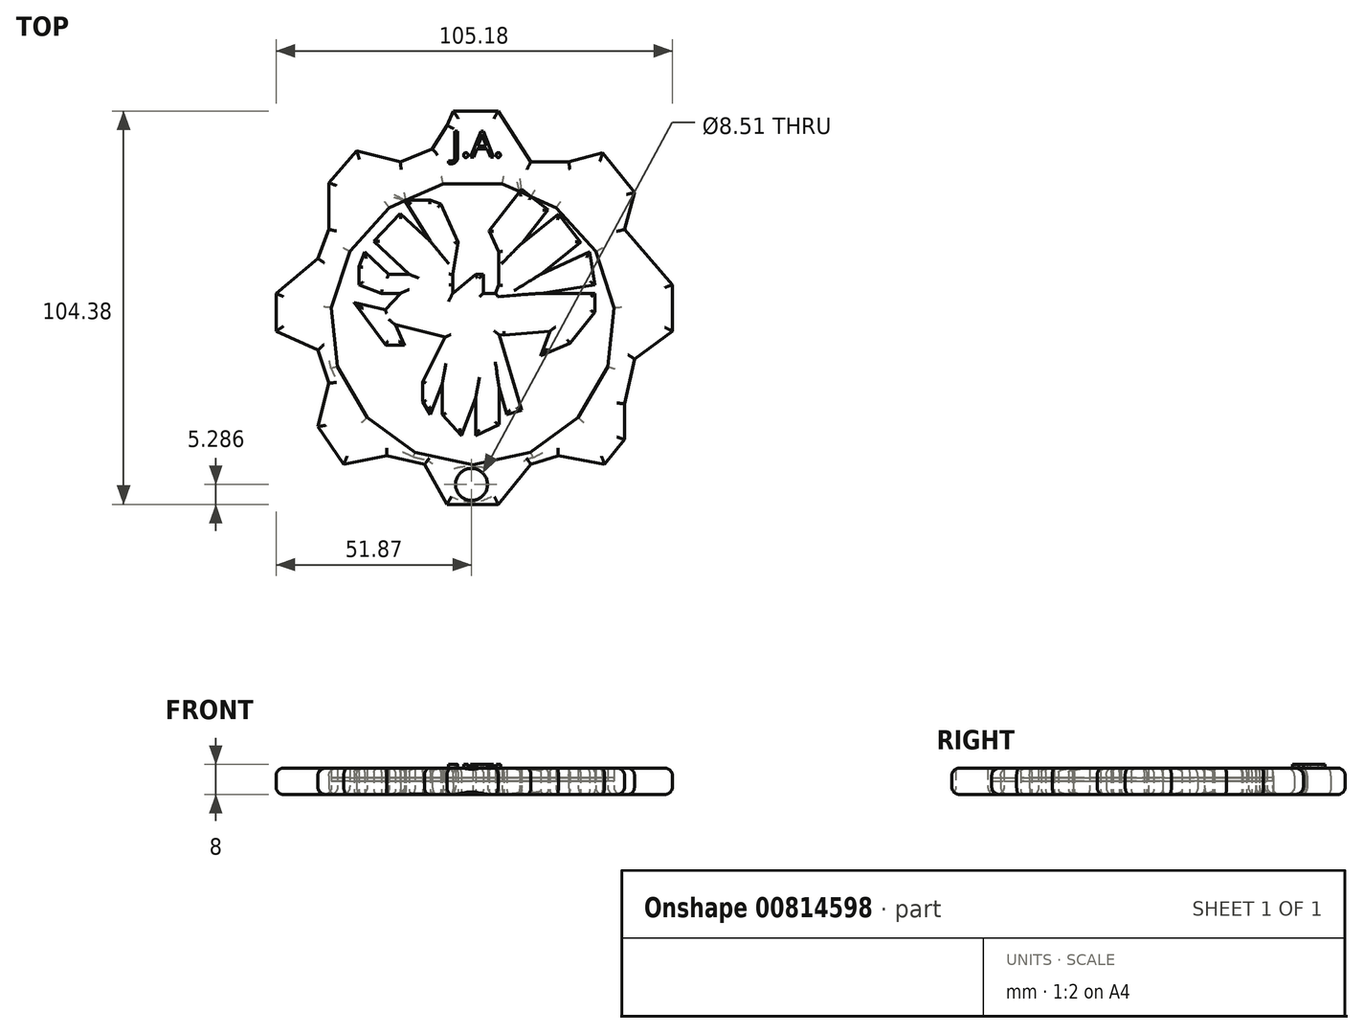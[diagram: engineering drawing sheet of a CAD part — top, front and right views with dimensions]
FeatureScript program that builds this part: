
annotation { "Feature Type Name" : "Feature", "Feature Type Description" : "" }
export const myFeature = defineFeature(function(context is Context, id is Id, definition is map)
    precondition{}
    {
        {
            var Q0;
            Q0=qCreatedBy(makeId("Top.planeOp"),FACE);
            var sketch = newSketch(context, id + "F0", { "sketchPlane" : qUnion([Q0])});
            skLineSegment(sketch, "E0", {"start": v(-27.88, 46.11) * mm, "end": v(-15.99, 46.11) * mm});
            skLineSegment(sketch, "E1", {"start": v(-15.99, 46.11) * mm, "end": v(-7.27, 32.64) * mm});
            skLineSegment(sketch, "E2", {"start": v(-7.27, 32.64) * mm, "end": v(2.77, 32.64) * mm});
            skLineSegment(sketch, "E3", {"start": v(2.77, 32.64) * mm, "end": v(11.76, 35.01) * mm});
            skLineSegment(sketch, "E4", {"start": v(11.76, 35.01) * mm, "end": v(20.22, 24.44) * mm});
            skLineSegment(sketch, "E5", {"start": v(20.22, 24.44) * mm, "end": v(17.57, 14.67) * mm});
            skLineSegment(sketch, "E6", {"start": v(17.57, 14.67) * mm, "end": v(30.26, 0) * mm});
            skLineSegment(sketch, "E7", {"start": v(30.26, 0) * mm, "end": v(30.26, -12.29) * mm});
            skLineSegment(sketch, "E8", {"start": v(30.26, -12.29) * mm, "end": v(20.22, -19.69) * mm});
            skLineSegment(sketch, "E9", {"start": v(20.22, -19.69) * mm, "end": v(17.57, -31.58) * mm});
            skLineSegment(sketch, "E10", {"start": v(17.57, -31.58) * mm, "end": v(17.57, -41.1) * mm});
            skLineSegment(sketch, "E11", {"start": v(17.57, -41.1) * mm, "end": v(12.29, -47.7) * mm});
            skLineSegment(sketch, "E12", {"start": v(12.29, -47.7) * mm, "end": v(0, -45.32) * mm});
            skLineSegment(sketch, "E13", {"start": v(0, -45.32) * mm, "end": v(-7.27, -47.7) * mm});
            skLineSegment(sketch, "E14", {"start": v(-7.27, -47.7) * mm, "end": v(-15.99, -58.27) * mm});
            skLineSegment(sketch, "E15", {"start": v(-15.99, -58.27) * mm, "end": v(-29.56, -58.27) * mm});
            skLineSegment(sketch, "E16", {"start": v(-29.56, -58.27) * mm, "end": v(-35.54, -47.7) * mm});
            skLineSegment(sketch, "E17", {"start": v(-35.54, -47.7) * mm, "end": v(-45.59, -45.32) * mm});
            skLineSegment(sketch, "E18", {"start": v(-45.59, -45.32) * mm, "end": v(-56.95, -47.7) * mm});
            skLineSegment(sketch, "E19", {"start": v(-56.95, -47.7) * mm, "end": v(-63.82, -37.66) * mm});
            skLineSegment(sketch, "E20", {"start": v(-63.82, -37.66) * mm, "end": v(-60.91, -26.03) * mm});
            skLineSegment(sketch, "E21", {"start": v(-60.91, -26.03) * mm, "end": v(-63.82, -17.3) * mm});
            skLineSegment(sketch, "E22", {"start": v(-63.82, -17.3) * mm, "end": v(-74.92, -12.29) * mm});
            skLineSegment(sketch, "E23", {"start": v(-74.92, -12.29) * mm, "end": v(-74.92, -2.25) * mm});
            skLineSegment(sketch, "E24", {"start": v(-74.92, -2.25) * mm, "end": v(-63.82, 7) * mm});
            skLineSegment(sketch, "E25", {"start": v(-63.82, 7) * mm, "end": v(-60.91, 14.67) * mm});
            skLineSegment(sketch, "E26", {"start": v(-60.91, 14.67) * mm, "end": v(-60.91, 27.09) * mm});
            skLineSegment(sketch, "E27", {"start": v(-60.91, 27.09) * mm, "end": v(-53.51, 35.54) * mm});
            skLineSegment(sketch, "E28", {"start": v(-53.51, 35.54) * mm, "end": v(-41.89, 32.64) * mm});
            skLineSegment(sketch, "E29", {"start": v(-41.89, 32.64) * mm, "end": v(-33.43, 36.07) * mm});
            skLineSegment(sketch, "E30", {"start": v(-33.43, 36.07) * mm, "end": v(-29.56, 42.33) * mm});
            skLineSegment(sketch, "E31", {"start": v(-29.56, 42.33) * mm, "end": v(-27.88, 46.11) * mm});
            skPoint(sketch, "E32.centerSnap0", {"position": v(-21.93, 46.11) * mm});
            skLineSegment(sketch, "E33", {"start": v(-30, -13.87) * mm, "end": v(-36.07, -25.77) * mm});
            skLineSegment(sketch, "E34", {"start": v(-36.07, -25.77) * mm, "end": v(-36.07, -31.05) * mm});
            skLineSegment(sketch, "E35", {"start": v(-36.07, -31.05) * mm, "end": v(-33.96, -34.49) * mm});
            skLineSegment(sketch, "E36", {"start": v(-33.96, -34.49) * mm, "end": v(-30.83, -26.24) * mm});
            skLineSegment(sketch, "E37", {"start": v(-30.83, -26.24) * mm, "end": v(-30.83, -34.49) * mm});
            skLineSegment(sketch, "E38", {"start": v(-30.83, -34.49) * mm, "end": v(-25.77, -40.04) * mm});
            skLineSegment(sketch, "E39", {"start": v(-25.77, -40.04) * mm, "end": v(-21.93, -29.93) * mm});
            skLineSegment(sketch, "E40", {"start": v(-21.93, -29.93) * mm, "end": v(-21.93, -40.04) * mm});
            skLineSegment(sketch, "E41", {"start": v(-21.93, -40.04) * mm, "end": v(-15.72, -37.13) * mm});
            skLineSegment(sketch, "E42", {"start": v(-15.72, -37.13) * mm, "end": v(-15.72, -27.35) * mm});
            skLineSegment(sketch, "E43", {"start": v(-15.72, -27.35) * mm, "end": v(-13.6, -34.49) * mm});
            skLineSegment(sketch, "E44", {"start": v(-13.6, -34.49) * mm, "end": v(-9.78, -33.35) * mm});
            skLineSegment(sketch, "E45", {"start": v(-9.78, -33.35) * mm, "end": v(-15.72, -13.28) * mm});
            skLineSegment(sketch, "E46", {"start": v(-15.72, -13.28) * mm, "end": v(-14.4, -13.35) * mm});
            skLineSegment(sketch, "E47", {"start": v(-2.25, -12.29) * mm, "end": v(-4.7, -18.77) * mm});
            skLineSegment(sketch, "E48", {"start": v(-4.7, -18.77) * mm, "end": v(3.04, -15.46) * mm});
            skLineSegment(sketch, "E49", {"start": v(3.04, -15.46) * mm, "end": v(9.65, -7.27) * mm});
            skLineSegment(sketch, "E50", {"start": v(9.65, -7.27) * mm, "end": v(9.65, -2.25) * mm});
            skLineSegment(sketch, "E51", {"start": v(9.65, -2.25) * mm, "end": v(-4.7, -2.25) * mm});
            skLineSegment(sketch, "E52", {"start": v(-4.7, -2.25) * mm, "end": v(9.65, 0) * mm});
            skLineSegment(sketch, "E53", {"start": v(9.65, 0) * mm, "end": v(8.28, 8.7) * mm});
            skLineSegment(sketch, "E54", {"start": v(8.28, 8.7) * mm, "end": v(-4.7, 2.77) * mm});
            skLineSegment(sketch, "E55", {"start": v(-4.7, 2.77) * mm, "end": v(5.95, 11.23) * mm});
            skLineSegment(sketch, "E56", {"start": v(5.95, 11.23) * mm, "end": v(0, 18.72) * mm});
            skLineSegment(sketch, "E57", {"start": v(0, 18.72) * mm, "end": v(-9.78, 10.96) * mm});
            skLineSegment(sketch, "E58", {"start": v(-9.78, 10.96) * mm, "end": v(-2.77, 19.95) * mm});
            skLineSegment(sketch, "E59", {"start": v(-2.77, 19.95) * mm, "end": v(-9.78, 25.4) * mm});
            skLineSegment(sketch, "E60", {"start": v(-9.78, 25.4) * mm, "end": v(-18.38, 14.35) * mm});
            skLineSegment(sketch, "E61", {"start": v(-18.38, 14.35) * mm, "end": v(-15.8, 8.7) * mm});
            skLineSegment(sketch, "E62", {"start": v(-15.8, 8.7) * mm, "end": v(-15.8, 0) * mm});
            skLineSegment(sketch, "E63", {"start": v(-15.8, 0) * mm, "end": v(-16.65, -2.25) * mm});
            skLineSegment(sketch, "E64", {"start": v(-16.65, -2.25) * mm, "end": v(-19.95, -2.25) * mm});
            skLineSegment(sketch, "E65", {"start": v(-19.95, -2.25) * mm, "end": v(-19.95, 2.77) * mm});
            skLineSegment(sketch, "E66", {"start": v(-19.95, 2.77) * mm, "end": v(-21.93, 2.77) * mm});
            skLineSegment(sketch, "E67", {"start": v(-28.01, 0) * mm, "end": v(-28.01, 2.77) * mm});
            skLineSegment(sketch, "E68", {"start": v(-28.01, 2.77) * mm, "end": v(-26.56, 11.23) * mm});
            skLineSegment(sketch, "E69", {"start": v(-26.56, 11.23) * mm, "end": v(-31.2, 21.4) * mm});
            skLineSegment(sketch, "E70", {"start": v(-31.2, 21.4) * mm, "end": v(-33.96, 22.44) * mm});
            skLineSegment(sketch, "E71", {"start": v(-33.96, 22.44) * mm, "end": v(-40.83, 22.44) * mm});
            skLineSegment(sketch, "E72", {"start": v(-40.83, 22.44) * mm, "end": v(-33.96, 11.5) * mm});
            skLineSegment(sketch, "E73", {"start": v(-33.96, 11.5) * mm, "end": v(-41.96, 18.96) * mm});
            skLineSegment(sketch, "E74", {"start": v(-41.96, 18.96) * mm, "end": v(-48.93, 11.5) * mm});
            skLineSegment(sketch, "E75", {"start": v(-48.93, 11.5) * mm, "end": v(-39.58, 2.77) * mm});
            skLineSegment(sketch, "E76", {"start": v(-39.58, 2.77) * mm, "end": v(-45.06, 2.77) * mm});
            skLineSegment(sketch, "E77", {"start": v(-45.06, 2.77) * mm, "end": v(-51.41, 8.7) * mm});
            skLineSegment(sketch, "E78", {"start": v(-51.41, 8.7) * mm, "end": v(-52.89, 4.82) * mm});
            skLineSegment(sketch, "E79", {"start": v(-52.89, 4.82) * mm, "end": v(-52.89, 0) * mm});
            skLineSegment(sketch, "E80", {"start": v(-52.89, 0) * mm, "end": v(-46.96, -2.25) * mm});
            skLineSegment(sketch, "E81", {"start": v(-46.96, -2.25) * mm, "end": v(-41.89, -2.25) * mm});
            skLineSegment(sketch, "E82", {"start": v(-41.89, -2.25) * mm, "end": v(-45.92, -6.57) * mm});
            skLineSegment(sketch, "E83", {"start": v(-45.92, -6.57) * mm, "end": v(-54.21, -4.73) * mm});
            skLineSegment(sketch, "E84", {"start": v(-54.21, -4.73) * mm, "end": v(-45.85, -15.99) * mm});
            skLineSegment(sketch, "E85", {"start": v(-45.85, -15.99) * mm, "end": v(-40.83, -15.99) * mm});
            skLineSegment(sketch, "E86", {"start": v(-40.83, -15.99) * mm, "end": v(-43.28, -10.62) * mm});
            skLineSegment(sketch, "E87", {"start": v(-43.28, -10.62) * mm, "end": v(-30, -13.87) * mm});
            skLineSegment(sketch, "E88", {"start": v(-14.4, -13.35) * mm, "end": v(-2.25, -12.29) * mm});
            skLineSegment(sketch, "E89", {"start": v(-21.93, 2.77) * mm, "end": v(-28.07, -2.25) * mm});
            skLineSegment(sketch, "E90", {"start": v(-28.07, -2.25) * mm, "end": v(-28.01, 0) * mm});
            skLineSegment(sketch, "E91", {"start": v(-40.83, 22.44) * mm, "end": v(-40.64, 22.18) * mm});
            skLineSegment(sketch, "E92", {"start": v(-40.64, 22.18) * mm, "end": v(-40.83, 22.44) * mm});
            skLineSegment(sketch, "E93", {"start": v(-9.85, 25.95) * mm, "end": v(-9.78, 25.4) * mm});
            skLineSegment(sketch, "E94", {"start": v(-9.78, 25.4) * mm, "end": v(-9.85, 25.95) * mm});
            skPoint(sketch, "E95.0.midPoint", {"position": v(-22.74, 30.9) * mm});
            skCircle(sketch, "E96.cCircle", {"center": v(-22.74, -10.03) * mm, "radius": 36.87 * mm, "construction": true});
            skLineSegment(sketch, "E96.0", {"start": v(-30.57, 26.83) * mm, "end": v(-14.9, 26.83) * mm});
            skLineSegment(sketch, "E96.1", {"start": v(-14.9, 26.83) * mm, "end": v(-0.58, 20.46) * mm});
            skLineSegment(sketch, "E96.2", {"start": v(-0.58, 20.46) * mm, "end": v(9.9, 8.81) * mm});
            skLineSegment(sketch, "E96.3", {"start": v(9.9, 8.81) * mm, "end": v(14.75, -6.1) * mm});
            skLineSegment(sketch, "E96.4", {"start": v(14.75, -6.1) * mm, "end": v(13.1, -21.68) * mm});
            skLineSegment(sketch, "E96.5", {"start": v(13.1, -21.68) * mm, "end": v(5.27, -35.25) * mm});
            skLineSegment(sketch, "E96.6", {"start": v(5.27, -35.25) * mm, "end": v(-7.4, -44.46) * mm});
            skLineSegment(sketch, "E96.7", {"start": v(-7.4, -44.46) * mm, "end": v(-22.74, -47.72) * mm});
            skLineSegment(sketch, "E96.8", {"start": v(-22.74, -47.72) * mm, "end": v(-38.07, -44.46) * mm});
            skLineSegment(sketch, "E96.9", {"start": v(-38.07, -44.46) * mm, "end": v(-50.75, -35.25) * mm});
            skLineSegment(sketch, "E96.10", {"start": v(-50.75, -35.25) * mm, "end": v(-58.58, -21.68) * mm});
            skLineSegment(sketch, "E96.11", {"start": v(-58.58, -21.68) * mm, "end": v(-60.22, -6.1) * mm});
            skLineSegment(sketch, "E96.12", {"start": v(-60.22, -6.1) * mm, "end": v(-55.38, 8.81) * mm});
            skLineSegment(sketch, "E96.13", {"start": v(-55.38, 8.81) * mm, "end": v(-44.9, 20.46) * mm});
            skLineSegment(sketch, "E96.14", {"start": v(-44.9, 20.46) * mm, "end": v(-30.57, 26.83) * mm});
            skPoint(sketch, "E96.0.midPoint", {"position": v(-22.74, 26.83) * mm});
            skCircle(sketch, "E97", {"center": v(-23.05, -52.98) * mm, "radius": 4.25 * mm});
            skPoint(sketch, "E97.centerSnap0", {"position": v(-11.63, -52.98) * mm});
            skSolve(sketch);
        }
        {
            var Q0;
            Q0=makeQuery(id+"F0.imprint","IMPRINT",FACE,{"disambiguationData":[TD([[makeQuery(id+"F0.imprint","IMPRINT",EDGE,{"derivedFrom":sQuery(id+"F0.wireOp",EDGE,"E0")}),-1.0]])]});
            var Q1;
            Q1=makeQuery(id+"F0.imprint","IMPRINT",FACE,{"disambiguationData":[TD([[makeQuery(id+"F0.imprint","IMPRINT",EDGE,{"derivedFrom":sQuery(id+"F0.wireOp",EDGE,"E33")}),1.0]])]});
            extrude(context, id + "F1", {"entities" : qUnion([Q0, Q1]), "endBound" : BoundingType.SYMMETRIC, "depth" : 7 * mm, "offsetDistance" : 25 * mm});
        }
        {
            var Q0;
            Q0=qCreatedBy(makeId("Top.planeOp"),FACE);
            var sketch = newSketch(context, id + "F2", { "sketchPlane" : qUnion([Q0])});
            skLineSegment(sketch, "E98", {"start": v(-41.91, 19.05) * mm, "end": v(-44.88, 20.46) * mm});
            skLineSegment(sketch, "E99", {"start": v(-44.88, 20.46) * mm, "end": v(-41.91, 19.05) * mm});
            skLineSegment(sketch, "E100", {"start": v(-48.9, 11.4) * mm, "end": v(-50.53, 14.16) * mm});
            skLineSegment(sketch, "E101", {"start": v(-50.53, 14.16) * mm, "end": v(-48.9, 11.4) * mm});
            skLineSegment(sketch, "E102", {"start": v(-31.2, 21.4) * mm, "end": v(-31.86, 26.3) * mm});
            skLineSegment(sketch, "E103", {"start": v(-31.86, 26.3) * mm, "end": v(-31.2, 21.4) * mm});
            skLineSegment(sketch, "E104", {"start": v(-12.53, 21.4) * mm, "end": v(-12.53, 26.18) * mm});
            skLineSegment(sketch, "E105", {"start": v(-12.53, 26.18) * mm, "end": v(-12.53, 21.4) * mm});
            skSolve(sketch);
        }
        {
            var Q0;
            Q0 = qSketchRegion(id + "F2", true);
            var Q1;
            Q1=makeQuery(id+"F0.imprint","IMPRINT",FACE,{"disambiguationData":[TD([[makeQuery(id+"F0.imprint","IMPRINT",EDGE,{"derivedFrom":sQuery(id+"F0.wireOp",EDGE,"E33")}),-1.0]])]});
            extrude(context, id + "F3", {"entities" : qUnion([Q0, Q1]), "depth" : 1 * mm, "offsetDistance" : 25 * mm});
        }
        {
            var Q0;
            Q0 = qSketchRegion(id + "F2", true);
            var Q1;
            {var subQ4=sQuery(id+"F0.wireOp",EDGE,"E61");Q1=makeQuery(id+"F0.imprint","IMPRINT",FACE,{"disambiguationData":[TD([[makeQuery(id+"F0.imprint","IMPRINT",EDGE,{"derivedFrom":subQ4}),-1.0]])]});}
            extrude(context, id + "F4", {"entities" : qUnion([Q0, Q1]), "depth" : 1 * mm, "offsetDistance" : 25 * mm});
        }
        {
            var Q0;
            Q0=sQuery(id+"F2.wireOp",EDGE,"E103");
            extrude(context, id + "F5", {"bodyType" : ToolBodyType.SURFACE, "surfaceEntities" : qUnion([Q0]), "depth" : 2 * mm, "offsetDistance" : 25 * mm});
        }
        {
            var Q0;
            Q0=makeQuery(id+"F1.opExtrude","CAP_FACE",FACE,{"disambiguationData":[OSD([sQuery(id+"F0.wireOp",EDGE,"E0"),sQuery(id+"F0.wireOp",EDGE,"E1"),sQuery(id+"F0.wireOp",EDGE,"E2"),sQuery(id+"F0.wireOp",EDGE,"E3"),sQuery(id+"F0.wireOp",EDGE,"E4"),sQuery(id+"F0.wireOp",EDGE,"E5"),sQuery(id+"F0.wireOp",EDGE,"E6"),sQuery(id+"F0.wireOp",EDGE,"E7"),sQuery(id+"F0.wireOp",EDGE,"E8"),sQuery(id+"F0.wireOp",EDGE,"E9"),sQuery(id+"F0.wireOp",EDGE,"E10"),sQuery(id+"F0.wireOp",EDGE,"E11"),sQuery(id+"F0.wireOp",EDGE,"E12"),sQuery(id+"F0.wireOp",EDGE,"E13"),sQuery(id+"F0.wireOp",EDGE,"E14"),sQuery(id+"F0.wireOp",EDGE,"E15"),sQuery(id+"F0.wireOp",EDGE,"E16"),sQuery(id+"F0.wireOp",EDGE,"E17"),sQuery(id+"F0.wireOp",EDGE,"E18"),sQuery(id+"F0.wireOp",EDGE,"E19"),sQuery(id+"F0.wireOp",EDGE,"E20"),sQuery(id+"F0.wireOp",EDGE,"E21"),sQuery(id+"F0.wireOp",EDGE,"E22"),sQuery(id+"F0.wireOp",EDGE,"E23"),sQuery(id+"F0.wireOp",EDGE,"E24"),sQuery(id+"F0.wireOp",EDGE,"E25"),sQuery(id+"F0.wireOp",EDGE,"E26"),sQuery(id+"F0.wireOp",EDGE,"E27"),sQuery(id+"F0.wireOp",EDGE,"E28"),sQuery(id+"F0.wireOp",EDGE,"E29"),sQuery(id+"F0.wireOp",EDGE,"E30"),sQuery(id+"F0.wireOp",EDGE,"E31"),sQuery(id+"F0.wireOp",EDGE,"E59"),sQuery(id+"F0.wireOp",EDGE,"E60"),sQuery(id+"F0.wireOp",EDGE,"E71"),sQuery(id+"F0.wireOp",EDGE,"E72"),sQuery(id+"F0.wireOp",EDGE,"E96.0"),sQuery(id+"F0.wireOp",EDGE,"E96.1"),sQuery(id+"F0.wireOp",EDGE,"E96.2"),sQuery(id+"F0.wireOp",EDGE,"E96.3"),sQuery(id+"F0.wireOp",EDGE,"E96.4"),sQuery(id+"F0.wireOp",EDGE,"E96.5"),sQuery(id+"F0.wireOp",EDGE,"E96.6"),sQuery(id+"F0.wireOp",EDGE,"E96.7"),sQuery(id+"F0.wireOp",EDGE,"E96.8"),sQuery(id+"F0.wireOp",EDGE,"E96.9"),sQuery(id+"F0.wireOp",EDGE,"E96.10"),sQuery(id+"F0.wireOp",EDGE,"E96.11"),sQuery(id+"F0.wireOp",EDGE,"E96.12"),sQuery(id+"F0.wireOp",EDGE,"E96.13"),sQuery(id+"F0.wireOp",EDGE,"E96.14")])],"isStart":false});
            var sketch = newSketch(context, id + "F6", { "sketchPlane" : qUnion([Q0])});
            skText(sketch, "E106", { "text": "J.A.\n", "fontName": "OpenSans-Regular.ttf"});
            const initialGuessF6  = {"E106": [-0.0284, 0.03393, 1, 0, 0.00691]};
            skSetInitialGuess(sketch, initialGuessF6);
            skSolve(sketch);
        }
        {
            var Q0;
            Q0 = qSketchRegion(id + "F6", true);
            extrude(context, id + "F7", {"entities" : qUnion([Q0]), "operationType" : NewBodyOperationType.ADD, "depth" : 1 * mm, "offsetDistance" : 25 * mm});
        }
        {
            var Q0;
            {var subQ0=sQuery(id+"F0.wireOp",EDGE,"E71");Q0=makeQuery(id+"F1.opExtrude","CAP_EDGE",EDGE,{"disambiguationData":[OSD([subQ0]),TDD([makeQuery(id+"F0.imprint","IMPRINT",EDGE,{"disambiguationData":[TD([[makeQuery(id+"F0.imprint","INTERSECT",VERTEX,{"derivedFrom":[sQuery(id+"F0.wireOp",EDGE,"E70"),subQ0]}),-1.0]])],"derivedFrom":subQ0})])],"isStart":false});}
            var Q1;
            Q1=makeQuery(id+"F1.opExtrude","CAP_EDGE",EDGE,{"disambiguationData":[OSD([sQuery(id+"F0.wireOp",EDGE,"E69")])],"isStart":false});
            var Q2;
            Q2=makeQuery(id+"F1.opExtrude","CAP_EDGE",EDGE,{"disambiguationData":[OSD([sQuery(id+"F0.wireOp",EDGE,"E89")])],"isStart":false});
            var Q3;
            {var subQ0=sQuery(id+"F0.wireOp",EDGE,"E60");Q3=makeQuery(id+"F1.opExtrude","CAP_EDGE",EDGE,{"disambiguationData":[OSD([subQ0]),TDD([makeQuery(id+"F0.imprint","IMPRINT",EDGE,{"disambiguationData":[TD([[makeQuery(id+"F0.imprint","INTERSECT",VERTEX,{"derivedFrom":[subQ0,sQuery(id+"F0.wireOp",EDGE,"E61")]}),1.0]])],"derivedFrom":subQ0})])],"isStart":false});}
            var Q4;
            Q4=makeQuery(id+"F1.opExtrude","CAP_EDGE",EDGE,{"disambiguationData":[OSD([sQuery(id+"F0.wireOp",EDGE,"E58")])],"isStart":false});
            var Q5;
            {var subQ0=sQuery(id+"F0.wireOp",EDGE,"E59");Q5=makeQuery(id+"F1.opExtrude","CAP_EDGE",EDGE,{"disambiguationData":[OSD([subQ0]),TDD([makeQuery(id+"F0.imprint","IMPRINT",EDGE,{"disambiguationData":[TD([[makeQuery(id+"F0.imprint","INTERSECT",VERTEX,{"derivedFrom":[sQuery(id+"F0.wireOp",EDGE,"E58"),subQ0]}),-1.0]])],"derivedFrom":subQ0})])],"isStart":false});}
            var Q6;
            Q6=makeQuery(id+"F1.opExtrude","CAP_EDGE",EDGE,{"disambiguationData":[OSD([sQuery(id+"F0.wireOp",EDGE,"E56")])],"isStart":false});
            var Q7;
            Q7=makeQuery(id+"F1.opExtrude","CAP_EDGE",EDGE,{"disambiguationData":[OSD([sQuery(id+"F0.wireOp",EDGE,"E57")])],"isStart":false});
            var Q8;
            Q8=makeQuery(id+"F1.opExtrude","CAP_EDGE",EDGE,{"disambiguationData":[OSD([sQuery(id+"F0.wireOp",EDGE,"E55")])],"isStart":false});
            var Q9;
            Q9=makeQuery(id+"F1.opExtrude","CAP_EDGE",EDGE,{"disambiguationData":[OSD([sQuery(id+"F0.wireOp",EDGE,"E54")])],"isStart":false});
            var Q10;
            Q10=makeQuery(id+"F1.opExtrude","CAP_EDGE",EDGE,{"disambiguationData":[OSD([sQuery(id+"F0.wireOp",EDGE,"E52")])],"isStart":false});
            var Q11;
            Q11=makeQuery(id+"F1.opExtrude","CAP_EDGE",EDGE,{"disambiguationData":[OSD([sQuery(id+"F0.wireOp",EDGE,"E53")])],"isStart":false});
            var Q12;
            Q12=makeQuery(id+"F1.opExtrude","CAP_EDGE",EDGE,{"disambiguationData":[OSD([sQuery(id+"F0.wireOp",EDGE,"E51")])],"isStart":false});
            var Q13;
            Q13=makeQuery(id+"F1.opExtrude","CAP_EDGE",EDGE,{"disambiguationData":[OSD([sQuery(id+"F0.wireOp",EDGE,"E50")])],"isStart":false});
            var Q14;
            Q14=makeQuery(id+"F1.opExtrude","CAP_EDGE",EDGE,{"disambiguationData":[OSD([sQuery(id+"F0.wireOp",EDGE,"E49")])],"isStart":false});
            var Q15;
            Q15=makeQuery(id+"F1.opExtrude","CAP_FACE",FACE,{"disambiguationData":[OSD([sQuery(id+"F0.wireOp",EDGE,"E33"),sQuery(id+"F0.wireOp",EDGE,"E34"),sQuery(id+"F0.wireOp",EDGE,"E35"),sQuery(id+"F0.wireOp",EDGE,"E36"),sQuery(id+"F0.wireOp",EDGE,"E37"),sQuery(id+"F0.wireOp",EDGE,"E38"),sQuery(id+"F0.wireOp",EDGE,"E39"),sQuery(id+"F0.wireOp",EDGE,"E40"),sQuery(id+"F0.wireOp",EDGE,"E41"),sQuery(id+"F0.wireOp",EDGE,"E42"),sQuery(id+"F0.wireOp",EDGE,"E43"),sQuery(id+"F0.wireOp",EDGE,"E44"),sQuery(id+"F0.wireOp",EDGE,"E45"),sQuery(id+"F0.wireOp",EDGE,"E46"),sQuery(id+"F0.wireOp",EDGE,"E47"),sQuery(id+"F0.wireOp",EDGE,"E48"),sQuery(id+"F0.wireOp",EDGE,"E49"),sQuery(id+"F0.wireOp",EDGE,"E50"),sQuery(id+"F0.wireOp",EDGE,"E51"),sQuery(id+"F0.wireOp",EDGE,"E52"),sQuery(id+"F0.wireOp",EDGE,"E53"),sQuery(id+"F0.wireOp",EDGE,"E54"),sQuery(id+"F0.wireOp",EDGE,"E55"),sQuery(id+"F0.wireOp",EDGE,"E56"),sQuery(id+"F0.wireOp",EDGE,"E57"),sQuery(id+"F0.wireOp",EDGE,"E58"),sQuery(id+"F0.wireOp",EDGE,"E59"),sQuery(id+"F0.wireOp",EDGE,"E60"),sQuery(id+"F0.wireOp",EDGE,"E61"),sQuery(id+"F0.wireOp",EDGE,"E62"),sQuery(id+"F0.wireOp",EDGE,"E63"),sQuery(id+"F0.wireOp",EDGE,"E64"),sQuery(id+"F0.wireOp",EDGE,"E65"),sQuery(id+"F0.wireOp",EDGE,"E66"),sQuery(id+"F0.wireOp",EDGE,"E67"),sQuery(id+"F0.wireOp",EDGE,"E68"),sQuery(id+"F0.wireOp",EDGE,"E69"),sQuery(id+"F0.wireOp",EDGE,"E70"),sQuery(id+"F0.wireOp",EDGE,"E71"),sQuery(id+"F0.wireOp",EDGE,"E72"),sQuery(id+"F0.wireOp",EDGE,"E73"),sQuery(id+"F0.wireOp",EDGE,"E74"),sQuery(id+"F0.wireOp",EDGE,"E75"),sQuery(id+"F0.wireOp",EDGE,"E76"),sQuery(id+"F0.wireOp",EDGE,"E77"),sQuery(id+"F0.wireOp",EDGE,"E78"),sQuery(id+"F0.wireOp",EDGE,"E79"),sQuery(id+"F0.wireOp",EDGE,"E80"),sQuery(id+"F0.wireOp",EDGE,"E81"),sQuery(id+"F0.wireOp",EDGE,"E82"),sQuery(id+"F0.wireOp",EDGE,"E83"),sQuery(id+"F0.wireOp",EDGE,"E84"),sQuery(id+"F0.wireOp",EDGE,"E85"),sQuery(id+"F0.wireOp",EDGE,"E86"),sQuery(id+"F0.wireOp",EDGE,"E87"),sQuery(id+"F0.wireOp",EDGE,"E88"),sQuery(id+"F0.wireOp",EDGE,"E89"),sQuery(id+"F0.wireOp",EDGE,"E90"),sQuery(id+"F0.wireOp",EDGE,"E96.1"),sQuery(id+"F0.wireOp",EDGE,"E96.14")])],"isStart":false});
            fillet(context, id + "F8", {"entities" : qUnion([Q0, Q1, Q2, Q3, Q4, Q5, Q6, Q7, Q8, Q9, Q10, Q11, Q12, Q13, Q14, Q15]), "radius" : 1 * mm, "tangentPropagation" : true, "allowEdgeOverflow" : false});
        }
        {
            var Q0;
            Q0=makeQuery(id+"F1.opExtrude","CAP_EDGE",EDGE,{"disambiguationData":[OSD([sQuery(id+"F0.wireOp",EDGE,"E27")])],"isStart":false});
            var Q1;
            Q1=makeQuery(id+"F1.opExtrude","CAP_EDGE",EDGE,{"disambiguationData":[OSD([sQuery(id+"F0.wireOp",EDGE,"E26")])],"isStart":false});
            var Q2;
            Q2=makeQuery(id+"F1.opExtrude","CAP_EDGE",EDGE,{"disambiguationData":[OSD([sQuery(id+"F0.wireOp",EDGE,"E25")])],"isStart":false});
            var Q3;
            Q3=makeQuery(id+"F1.opExtrude","CAP_EDGE",EDGE,{"disambiguationData":[OSD([sQuery(id+"F0.wireOp",EDGE,"E24")])],"isStart":false});
            var Q4;
            Q4=makeQuery(id+"F1.opExtrude","CAP_EDGE",EDGE,{"disambiguationData":[OSD([sQuery(id+"F0.wireOp",EDGE,"E23")])],"isStart":false});
            var Q5;
            Q5=makeQuery(id+"F1.opExtrude","CAP_EDGE",EDGE,{"disambiguationData":[OSD([sQuery(id+"F0.wireOp",EDGE,"E22")])],"isStart":false});
            var Q6;
            Q6=makeQuery(id+"F1.opExtrude","CAP_EDGE",EDGE,{"disambiguationData":[OSD([sQuery(id+"F0.wireOp",EDGE,"E21")])],"isStart":false});
            var Q7;
            Q7=makeQuery(id+"F1.opExtrude","CAP_EDGE",EDGE,{"disambiguationData":[OSD([sQuery(id+"F0.wireOp",EDGE,"E20")])],"isStart":false});
            var Q8;
            Q8=makeQuery(id+"F1.opExtrude","CAP_EDGE",EDGE,{"disambiguationData":[OSD([sQuery(id+"F0.wireOp",EDGE,"E19")])],"isStart":false});
            var Q9;
            Q9=makeQuery(id+"F1.opExtrude","CAP_EDGE",EDGE,{"disambiguationData":[OSD([sQuery(id+"F0.wireOp",EDGE,"E18")])],"isStart":false});
            var Q10;
            Q10=makeQuery(id+"F1.opExtrude","CAP_EDGE",EDGE,{"disambiguationData":[OSD([sQuery(id+"F0.wireOp",EDGE,"E17")])],"isStart":false});
            var Q11;
            Q11=makeQuery(id+"F1.opExtrude","CAP_EDGE",EDGE,{"disambiguationData":[OSD([sQuery(id+"F0.wireOp",EDGE,"E16")])],"isStart":false});
            var Q12;
            Q12=makeQuery(id+"F1.opExtrude","CAP_EDGE",EDGE,{"disambiguationData":[OSD([sQuery(id+"F0.wireOp",EDGE,"E15")])],"isStart":false});
            var Q13;
            Q13=makeQuery(id+"F1.opExtrude","CAP_EDGE",EDGE,{"disambiguationData":[OSD([sQuery(id+"F0.wireOp",EDGE,"E14")])],"isStart":false});
            var Q14;
            Q14=makeQuery(id+"F1.opExtrude","CAP_EDGE",EDGE,{"disambiguationData":[OSD([sQuery(id+"F0.wireOp",EDGE,"E13")])],"isStart":false});
            var Q15;
            Q15=makeQuery(id+"F1.opExtrude","CAP_EDGE",EDGE,{"disambiguationData":[OSD([sQuery(id+"F0.wireOp",EDGE,"E11")])],"isStart":false});
            var Q16;
            Q16=makeQuery(id+"F1.opExtrude","CAP_EDGE",EDGE,{"disambiguationData":[OSD([sQuery(id+"F0.wireOp",EDGE,"E12")])],"isStart":false});
            var Q17;
            Q17=makeQuery(id+"F1.opExtrude","CAP_EDGE",EDGE,{"disambiguationData":[OSD([sQuery(id+"F0.wireOp",EDGE,"E9")])],"isStart":false});
            var Q18;
            Q18=makeQuery(id+"F1.opExtrude","CAP_EDGE",EDGE,{"disambiguationData":[OSD([sQuery(id+"F0.wireOp",EDGE,"E8")])],"isStart":false});
            var Q19;
            Q19=makeQuery(id+"F1.opExtrude","CAP_EDGE",EDGE,{"disambiguationData":[OSD([sQuery(id+"F0.wireOp",EDGE,"E7")])],"isStart":false});
            var Q20;
            Q20=makeQuery(id+"F1.opExtrude","CAP_EDGE",EDGE,{"disambiguationData":[OSD([sQuery(id+"F0.wireOp",EDGE,"E6")])],"isStart":false});
            var Q21;
            Q21=makeQuery(id+"F1.opExtrude","CAP_EDGE",EDGE,{"disambiguationData":[OSD([sQuery(id+"F0.wireOp",EDGE,"E5")])],"isStart":false});
            var Q22;
            Q22=makeQuery(id+"F1.opExtrude","CAP_EDGE",EDGE,{"disambiguationData":[OSD([sQuery(id+"F0.wireOp",EDGE,"E4")])],"isStart":false});
            var Q23;
            Q23=makeQuery(id+"F1.opExtrude","CAP_EDGE",EDGE,{"disambiguationData":[OSD([sQuery(id+"F0.wireOp",EDGE,"E10")])],"isStart":false});
            var Q24;
            Q24=makeQuery(id+"F1.opExtrude","CAP_EDGE",EDGE,{"disambiguationData":[OSD([sQuery(id+"F0.wireOp",EDGE,"E28")])],"isStart":false});
            var Q25;
            Q25=makeQuery(id+"F1.opExtrude","CAP_EDGE",EDGE,{"disambiguationData":[OSD([sQuery(id+"F0.wireOp",EDGE,"E29")])],"isStart":false});
            var Q26;
            Q26=makeQuery(id+"F1.opExtrude","CAP_EDGE",EDGE,{"disambiguationData":[OSD([sQuery(id+"F0.wireOp",EDGE,"E30")])],"isStart":false});
            var Q27;
            Q27=makeQuery(id+"F1.opExtrude","CAP_EDGE",EDGE,{"disambiguationData":[OSD([sQuery(id+"F0.wireOp",EDGE,"E0")])],"isStart":false});
            var Q28;
            Q28=makeQuery(id+"F1.opExtrude","CAP_EDGE",EDGE,{"disambiguationData":[OSD([sQuery(id+"F0.wireOp",EDGE,"E31")])],"isStart":false});
            var Q29;
            Q29=makeQuery(id+"F1.opExtrude","CAP_EDGE",EDGE,{"disambiguationData":[OSD([sQuery(id+"F0.wireOp",EDGE,"E1")])],"isStart":false});
            var Q30;
            Q30=makeQuery(id+"F1.opExtrude","CAP_EDGE",EDGE,{"disambiguationData":[OSD([sQuery(id+"F0.wireOp",EDGE,"E2")])],"isStart":false});
            var Q31;
            Q31=makeQuery(id+"F1.opExtrude","CAP_EDGE",EDGE,{"disambiguationData":[OSD([sQuery(id+"F0.wireOp",EDGE,"E3")])],"isStart":false});
            var Q32;
            Q32=makeQuery(id+"F1.opExtrude","CAP_FACE",FACE,{"disambiguationData":[OSD([sQuery(id+"F0.wireOp",EDGE,"E0"),sQuery(id+"F0.wireOp",EDGE,"E1"),sQuery(id+"F0.wireOp",EDGE,"E2"),sQuery(id+"F0.wireOp",EDGE,"E3"),sQuery(id+"F0.wireOp",EDGE,"E4"),sQuery(id+"F0.wireOp",EDGE,"E5"),sQuery(id+"F0.wireOp",EDGE,"E6"),sQuery(id+"F0.wireOp",EDGE,"E7"),sQuery(id+"F0.wireOp",EDGE,"E8"),sQuery(id+"F0.wireOp",EDGE,"E9"),sQuery(id+"F0.wireOp",EDGE,"E10"),sQuery(id+"F0.wireOp",EDGE,"E11"),sQuery(id+"F0.wireOp",EDGE,"E12"),sQuery(id+"F0.wireOp",EDGE,"E13"),sQuery(id+"F0.wireOp",EDGE,"E14"),sQuery(id+"F0.wireOp",EDGE,"E15"),sQuery(id+"F0.wireOp",EDGE,"E16"),sQuery(id+"F0.wireOp",EDGE,"E17"),sQuery(id+"F0.wireOp",EDGE,"E18"),sQuery(id+"F0.wireOp",EDGE,"E19"),sQuery(id+"F0.wireOp",EDGE,"E20"),sQuery(id+"F0.wireOp",EDGE,"E21"),sQuery(id+"F0.wireOp",EDGE,"E22"),sQuery(id+"F0.wireOp",EDGE,"E23"),sQuery(id+"F0.wireOp",EDGE,"E24"),sQuery(id+"F0.wireOp",EDGE,"E25"),sQuery(id+"F0.wireOp",EDGE,"E26"),sQuery(id+"F0.wireOp",EDGE,"E27"),sQuery(id+"F0.wireOp",EDGE,"E28"),sQuery(id+"F0.wireOp",EDGE,"E29"),sQuery(id+"F0.wireOp",EDGE,"E30"),sQuery(id+"F0.wireOp",EDGE,"E31"),sQuery(id+"F0.wireOp",EDGE,"E59"),sQuery(id+"F0.wireOp",EDGE,"E60"),sQuery(id+"F0.wireOp",EDGE,"E71"),sQuery(id+"F0.wireOp",EDGE,"E72"),sQuery(id+"F0.wireOp",EDGE,"E96.0"),sQuery(id+"F0.wireOp",EDGE,"E96.1"),sQuery(id+"F0.wireOp",EDGE,"E96.2"),sQuery(id+"F0.wireOp",EDGE,"E96.3"),sQuery(id+"F0.wireOp",EDGE,"E96.4"),sQuery(id+"F0.wireOp",EDGE,"E96.5"),sQuery(id+"F0.wireOp",EDGE,"E96.6"),sQuery(id+"F0.wireOp",EDGE,"E96.7"),sQuery(id+"F0.wireOp",EDGE,"E96.8"),sQuery(id+"F0.wireOp",EDGE,"E96.9"),sQuery(id+"F0.wireOp",EDGE,"E96.10"),sQuery(id+"F0.wireOp",EDGE,"E96.11"),sQuery(id+"F0.wireOp",EDGE,"E96.12"),sQuery(id+"F0.wireOp",EDGE,"E96.13"),sQuery(id+"F0.wireOp",EDGE,"E96.14")])],"isStart":true});
            fillet(context, id + "F9", {"entities" : qUnion([Q0, Q1, Q2, Q3, Q4, Q5, Q6, Q7, Q8, Q9, Q10, Q11, Q12, Q13, Q14, Q15, Q16, Q17, Q18, Q19, Q20, Q21, Q22, Q23, Q24, Q25, Q26, Q27, Q28, Q29, Q30, Q31, Q32]), "radius" : 2 * mm, "tangentPropagation" : true, "allowEdgeOverflow" : false});
        }
        {
            var Q0;
            {var subQ0=sQuery(id+"F0.wireOp",EDGE,"E60");Q0=makeQuery(id+"F1.opExtrude","CAP_EDGE",EDGE,{"disambiguationData":[OSD([subQ0]),TDD([makeQuery(id+"F0.imprint","IMPRINT",EDGE,{"disambiguationData":[TD([[makeQuery(id+"F0.imprint","INTERSECT",VERTEX,{"derivedFrom":[subQ0,sQuery(id+"F0.wireOp",EDGE,"E61")]}),1.0]])],"derivedFrom":subQ0})])],"isStart":true});}
            var Q1;
            Q1=makeQuery(id+"F1.opExtrude","CAP_EDGE",EDGE,{"disambiguationData":[OSD([sQuery(id+"F0.wireOp",EDGE,"E58")])],"isStart":true});
            var Q2;
            Q2=makeQuery(id+"F1.opExtrude","CAP_EDGE",EDGE,{"disambiguationData":[OSD([sQuery(id+"F0.wireOp",EDGE,"E57")])],"isStart":true});
            var Q3;
            Q3=makeQuery(id+"F1.opExtrude","CAP_EDGE",EDGE,{"disambiguationData":[OSD([sQuery(id+"F0.wireOp",EDGE,"E55")])],"isStart":true});
            var Q4;
            Q4=makeQuery(id+"F1.opExtrude","CAP_EDGE",EDGE,{"disambiguationData":[OSD([sQuery(id+"F0.wireOp",EDGE,"E56")])],"isStart":true});
            var Q5;
            Q5=makeQuery(id+"F1.opExtrude","CAP_EDGE",EDGE,{"disambiguationData":[OSD([sQuery(id+"F0.wireOp",EDGE,"E54")])],"isStart":true});
            var Q6;
            Q6=makeQuery(id+"F1.opExtrude","CAP_EDGE",EDGE,{"disambiguationData":[OSD([sQuery(id+"F0.wireOp",EDGE,"E53")])],"isStart":true});
            var Q7;
            Q7=makeQuery(id+"F1.opExtrude","CAP_FACE",FACE,{"disambiguationData":[OSD([sQuery(id+"F0.wireOp",EDGE,"E33"),sQuery(id+"F0.wireOp",EDGE,"E34"),sQuery(id+"F0.wireOp",EDGE,"E35"),sQuery(id+"F0.wireOp",EDGE,"E36"),sQuery(id+"F0.wireOp",EDGE,"E37"),sQuery(id+"F0.wireOp",EDGE,"E38"),sQuery(id+"F0.wireOp",EDGE,"E39"),sQuery(id+"F0.wireOp",EDGE,"E40"),sQuery(id+"F0.wireOp",EDGE,"E41"),sQuery(id+"F0.wireOp",EDGE,"E42"),sQuery(id+"F0.wireOp",EDGE,"E43"),sQuery(id+"F0.wireOp",EDGE,"E44"),sQuery(id+"F0.wireOp",EDGE,"E45"),sQuery(id+"F0.wireOp",EDGE,"E46"),sQuery(id+"F0.wireOp",EDGE,"E47"),sQuery(id+"F0.wireOp",EDGE,"E48"),sQuery(id+"F0.wireOp",EDGE,"E49"),sQuery(id+"F0.wireOp",EDGE,"E50"),sQuery(id+"F0.wireOp",EDGE,"E51"),sQuery(id+"F0.wireOp",EDGE,"E52"),sQuery(id+"F0.wireOp",EDGE,"E53"),sQuery(id+"F0.wireOp",EDGE,"E54"),sQuery(id+"F0.wireOp",EDGE,"E55"),sQuery(id+"F0.wireOp",EDGE,"E56"),sQuery(id+"F0.wireOp",EDGE,"E57"),sQuery(id+"F0.wireOp",EDGE,"E58"),sQuery(id+"F0.wireOp",EDGE,"E59"),sQuery(id+"F0.wireOp",EDGE,"E60"),sQuery(id+"F0.wireOp",EDGE,"E61"),sQuery(id+"F0.wireOp",EDGE,"E62"),sQuery(id+"F0.wireOp",EDGE,"E63"),sQuery(id+"F0.wireOp",EDGE,"E64"),sQuery(id+"F0.wireOp",EDGE,"E65"),sQuery(id+"F0.wireOp",EDGE,"E66"),sQuery(id+"F0.wireOp",EDGE,"E67"),sQuery(id+"F0.wireOp",EDGE,"E68"),sQuery(id+"F0.wireOp",EDGE,"E69"),sQuery(id+"F0.wireOp",EDGE,"E70"),sQuery(id+"F0.wireOp",EDGE,"E71"),sQuery(id+"F0.wireOp",EDGE,"E72"),sQuery(id+"F0.wireOp",EDGE,"E73"),sQuery(id+"F0.wireOp",EDGE,"E74"),sQuery(id+"F0.wireOp",EDGE,"E75"),sQuery(id+"F0.wireOp",EDGE,"E76"),sQuery(id+"F0.wireOp",EDGE,"E77"),sQuery(id+"F0.wireOp",EDGE,"E78"),sQuery(id+"F0.wireOp",EDGE,"E79"),sQuery(id+"F0.wireOp",EDGE,"E80"),sQuery(id+"F0.wireOp",EDGE,"E81"),sQuery(id+"F0.wireOp",EDGE,"E82"),sQuery(id+"F0.wireOp",EDGE,"E83"),sQuery(id+"F0.wireOp",EDGE,"E84"),sQuery(id+"F0.wireOp",EDGE,"E85"),sQuery(id+"F0.wireOp",EDGE,"E86"),sQuery(id+"F0.wireOp",EDGE,"E87"),sQuery(id+"F0.wireOp",EDGE,"E88"),sQuery(id+"F0.wireOp",EDGE,"E89"),sQuery(id+"F0.wireOp",EDGE,"E90"),sQuery(id+"F0.wireOp",EDGE,"E96.1"),sQuery(id+"F0.wireOp",EDGE,"E96.14")])],"isStart":true});
            fillet(context, id + "F10", {"entities" : qUnion([Q0, Q1, Q2, Q3, Q4, Q5, Q6, Q7]), "radius" : 1 * mm, "tangentPropagation" : true, "allowEdgeOverflow" : false});
        }
    });
